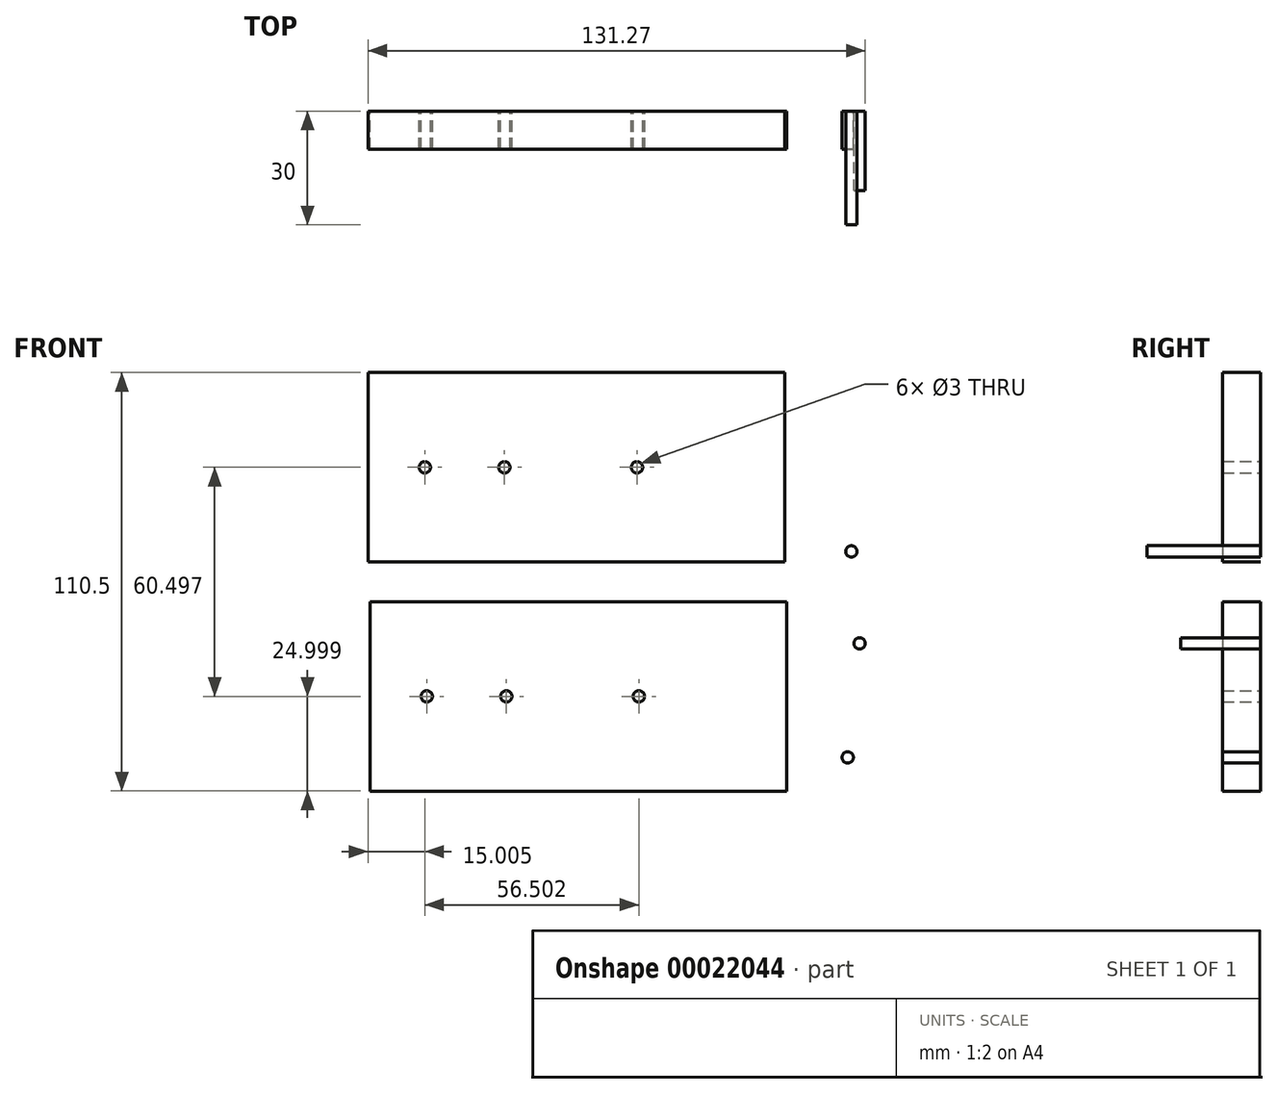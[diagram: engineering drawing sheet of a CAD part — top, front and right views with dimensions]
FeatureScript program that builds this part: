
annotation { "Feature Type Name" : "Feature", "Feature Type Description" : "" }
export const myFeature = defineFeature(function(context is Context, id is Id, definition is map)
    precondition{}
    {
        {
            var Q0;
            Q0=qCreatedBy(makeId("Front.planeOp"),FACE);
            var sketch = newSketch(context, id + "F0", { "sketchPlane" : qUnion([Q0])});
            skLineSegment(sketch, "E0.bottom", {"start": v(-80.44, 14.84) * mm, "end": v(29.56, 14.84) * mm});
            skLineSegment(sketch, "E0.top", {"start": v(-80.44, -35.16) * mm, "end": v(29.56, -35.16) * mm});
            skLineSegment(sketch, "E0.left", {"start": v(-80.44, 14.84) * mm, "end": v(-80.44, -35.16) * mm});
            skLineSegment(sketch, "E0.right", {"start": v(29.56, 14.84) * mm, "end": v(29.56, -35.16) * mm});
            skCircle(sketch, "E1", {"center": v(46.63, 28.12) * mm, "radius": 1.5 * mm});
            skLineSegment(sketch, "E2.bottom", {"start": v(-80.95, 75.34) * mm, "end": v(29.05, 75.34) * mm});
            skLineSegment(sketch, "E2.top", {"start": v(-80.95, 25.34) * mm, "end": v(29.05, 25.34) * mm});
            skLineSegment(sketch, "E2.left", {"start": v(-80.95, 75.34) * mm, "end": v(-80.95, 25.34) * mm});
            skLineSegment(sketch, "E2.right", {"start": v(29.05, 75.34) * mm, "end": v(29.05, 25.34) * mm});
            skPoint(sketch, "E3", {"position": v(-25.95, 50.34) * mm});
            skPoint(sketch, "E4.orphan", {"position": v(-25.95, 75.34) * mm});
            skPoint(sketch, "E5.orphan", {"position": v(29.05, 50.34) * mm});
            skPoint(sketch, "E6.end.orphan", {"position": v(-25.95, 25.34) * mm});
            skPoint(sketch, "E7.start.orphan", {"position": v(-80.95, 50.34) * mm});
            skPoint(sketch, "E8.orphan", {"position": v(-25.44, 14.84) * mm});
            skPoint(sketch, "E9.orphan", {"position": v(29.56, -10.16) * mm});
            skPoint(sketch, "E10.end.orphan", {"position": v(-25.44, -35.16) * mm});
            skPoint(sketch, "E11.start.orphan", {"position": v(-80.44, -10.16) * mm});
            skCircle(sketch, "E12", {"center": v(48.82, 3.84) * mm, "radius": 1.5 * mm});
            skCircle(sketch, "E13", {"center": v(45.69, -26.28) * mm, "radius": 1.5 * mm});
            skPoint(sketch, "E14", {"position": v(-65.95, 50.34) * mm});
            skPoint(sketch, "E15", {"position": v(-44.95, 50.34) * mm});
            skPoint(sketch, "E16", {"position": v(-65.44, -10.16) * mm});
            skPoint(sketch, "E17", {"position": v(-44.44, -10.16) * mm});
            skCircle(sketch, "E18", {"center": v(-65.95, 50.34) * mm, "radius": 1.5 * mm});
            skCircle(sketch, "E19", {"center": v(-65.44, -10.16) * mm, "radius": 1.5 * mm});
            skCircle(sketch, "E20", {"center": v(-44.44, -10.16) * mm, "radius": 1.5 * mm});
            skCircle(sketch, "E21", {"center": v(-44.95, 50.34) * mm, "radius": 1.5 * mm});
            skLineSegment(sketch, "E22", {"start": v(-80.95, 50.34) * mm, "end": v(29.05, 50.34) * mm});
            skLineSegment(sketch, "E23", {"start": v(-80.44, -10.16) * mm, "end": v(29.56, -10.16) * mm});
            skPoint(sketch, "E24", {"position": v(-9.95, 50.34) * mm});
            skPoint(sketch, "E25", {"position": v(-9.44, -10.16) * mm});
            skCircle(sketch, "E26", {"center": v(-9.44, -10.16) * mm, "radius": 1.5 * mm});
            skCircle(sketch, "E27", {"center": v(-9.95, 50.34) * mm, "radius": 1.5 * mm});
            skSolve(sketch);
        }
        {
            var Q0;
            Q0 = qSketchRegion(id + "F0", true);
            var Q1;
            Q1=makeQuery(id+"F0.imprint","IMPRINT",FACE,{"disambiguationData":[TD([[makeQuery(id+"F0.imprint","IMPRINT",EDGE,{"derivedFrom":sQuery(id+"F0.wireOp",EDGE,"E0.bottom")}),-1.0]])]});
            extrude(context, id + "F1", {"entities" : qUnion([Q0, Q1]), "depth" : 10 * mm});
        }
        {
            var Q0;
            Q0=makeQuery(id+"F0.imprint","IMPRINT",FACE,{"disambiguationData":[TD([[makeQuery(id+"F0.imprint","IMPRINT",EDGE,{"derivedFrom":sQuery(id+"F0.wireOp",EDGE,"E1")}),1.0]])]});
            extrude(context, id + "F2", {"entities" : qUnion([Q0]), "operationType" : NewBodyOperationType.ADD, "depth" : 30 * mm});
        }
        {
            var Q0;
            Q0=makeQuery(id+"F0.imprint","IMPRINT",FACE,{"disambiguationData":[TD([[makeQuery(id+"F0.imprint","IMPRINT",EDGE,{"derivedFrom":sQuery(id+"F0.wireOp",EDGE,"E12")}),1.0]])]});
            extrude(context, id + "F3", {"entities" : qUnion([Q0]), "operationType" : NewBodyOperationType.ADD, "depth" : 21 * mm});
        }
        {
            var Q0;
            Q0=makeQuery(id+"F1.opExtrude","CAP_FACE",FACE,{"disambiguationData":[OSD([sQuery(id+"F0.wireOp",EDGE,"E13")])],"isStart":false});
            extrude(context, id + "F4", {"entities" : qUnion([Q0]), "operationType" : NewBodyOperationType.REMOVE, "depth" : 1 * mm});
        }
    });
